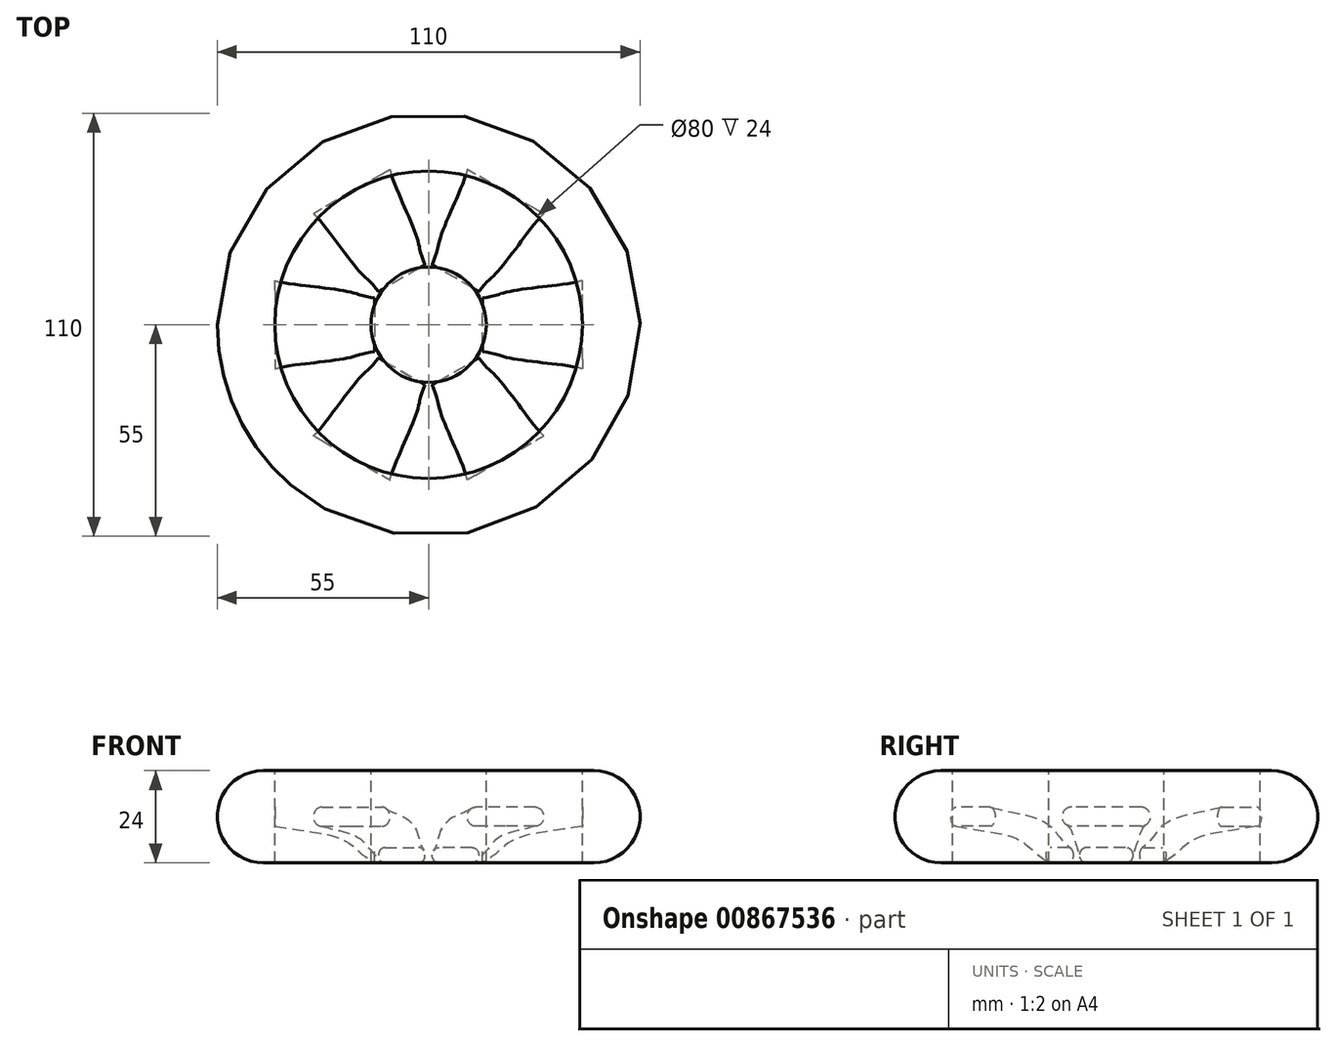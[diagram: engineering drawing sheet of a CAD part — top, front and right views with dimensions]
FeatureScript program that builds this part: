
annotation { "Feature Type Name" : "Feature", "Feature Type Description" : "" }
export const myFeature = defineFeature(function(context is Context, id is Id, definition is map)
    precondition{}
    {
        {
            var Q0;
            Q0=qCreatedBy(makeId("Top.planeOp"),FACE);
            var sketch = newSketch(context, id + "F0", { "sketchPlane" : qUnion([Q0])});
            skCircle(sketch, "E0", {"center": v(0, 0) * mm, "radius": 40 * mm});
            skSolve(sketch);
        }
        {
            var Q0;
            Q0=qCreatedBy(makeId("Front.planeOp"),FACE);
            var sketch = newSketch(context, id + "F1", { "sketchPlane" : qUnion([Q0])});
            skArc(sketch, "E1", {"start": v(-43, 12) * mm, "mid": v(-55, 0) * mm, "end": v(-43, -12) * mm});
            skLineSegment(sketch, "E2.bottom", {"start": v(-43, 12) * mm, "end": v(-40, 12) * mm});
            skLineSegment(sketch, "E2.top", {"start": v(-43, -12) * mm, "end": v(-40, -12) * mm});
            skLineSegment(sketch, "E2.right", {"start": v(-40, 12) * mm, "end": v(-40, -12) * mm});
            skSolve(sketch);
        }
        {
            var Q0;
            Q0 = qSketchRegion(id + "F1", true);
            var Q1;
            Q1=sQuery(id+"F0.wireOp",EDGE,"E0");
            sweep(context, id + "F2", {"profiles" : qUnion([Q0]), "path" : qUnion([Q1])});
        }
        {
            var Q0;
            Q0=qCreatedBy(makeId("Right.planeOp"),FACE);
            cPlane(context, id + "F3", {"entities" : qUnion([Q0]), "cplaneType" : CPlaneType.OFFSET, "offset" : 40 * mm, "width" : 150 * mm, "height" : 150 * mm});
        }
        {
            var Q0;
            Q0=qCreatedBy(id+"F3.planeOp",FACE);
            var sketch = newSketch(context, id + "F4", { "sketchPlane" : qUnion([Q0])});
            skLineSegment(sketch, "E3", {"start": v(-9, 0) * mm, "end": v(9, 0) * mm});
            skArc(sketch, "E4.0.startCap", {"start": v(-9, -2.5) * mm, "mid": v(-11.5, 0) * mm, "end": v(-9, 2.5) * mm});
            skArc(sketch, "E4.0.endCap", {"start": v(9, 2.5) * mm, "mid": v(11.5, 0) * mm, "end": v(9, -2.5) * mm});
            skLineSegment(sketch, "E4.0.left", {"start": v(-9, 2.5) * mm, "end": v(9, 2.5) * mm});
            skLineSegment(sketch, "E4.0.right", {"start": v(-9, -2.5) * mm, "end": v(9, -2.5) * mm});
            skSolve(sketch);
        }
        {
            var Q0;
            Q0=qCreatedBy(makeId("Right.planeOp"),FACE);
            cPlane(context, id + "F5", {"entities" : qUnion([Q0]), "cplaneType" : CPlaneType.OFFSET, "offset" : 14 * mm, "width" : 150 * mm, "height" : 150 * mm});
        }
        {
            var Q0;
            Q0=qCreatedBy(id+"F5.planeOp",FACE);
            var sketch = newSketch(context, id + "F6", { "sketchPlane" : qUnion([Q0])});
            skLineSegment(sketch, "E5", {"start": v(-5, -10) * mm, "end": v(5, -10) * mm});
            skArc(sketch, "E6.0.startCap", {"start": v(-5, -12) * mm, "mid": v(-7, -10) * mm, "end": v(-5, -8) * mm});
            skArc(sketch, "E6.0.endCap", {"start": v(5, -8) * mm, "mid": v(7, -10) * mm, "end": v(5, -12) * mm});
            skLineSegment(sketch, "E6.0.left", {"start": v(-5, -8) * mm, "end": v(5, -8) * mm});
            skLineSegment(sketch, "E6.0.right", {"start": v(-5, -12) * mm, "end": v(5, -12) * mm});
            skSolve(sketch);
        }
        {
            var Q0;
            Q0=qCreatedBy(makeId("Front.planeOp"),FACE);
            var sketch = newSketch(context, id + "F7", { "sketchPlane" : qUnion([Q0])});
            skFitSpline(sketch, "E7", {"points": [v(40, -2.5) * mm, v(35.5, -3.19) * mm, v(23.17, -5.57) * mm, v(18.78, -8.46) * mm, v(14, -12) * mm], "startDerivative": vector(-12, -0.82) * mm, "endDerivative": vector(-37, -22.75) * mm});
            skSolve(sketch);
        }
        {
            var Q1;
            Q1 = qSketchRegion(id + "F4", true);
            var Q2;
            Q2 = qSketchRegion(id + "F6", true);
            var Q3;
            Q3=sQuery(id+"F7.wireOp",EDGE,"E7");
            loft(context, id + "F8", {"addGuides" : true, "sheetProfilesArray" : [{ "sheetProfileEntities" : qUnion([Q1]) }, { "sheetProfileEntities" : qUnion([Q2]) }], "guidesArray" : [{ "guideEntities" : qUnion([Q3]), "guideDerivativeType" : LoftGuideDerivativeType.DEFAULT, "guideDerivativeMagnitude" : 1 }]});
        }
        {
            var Q0;
            Q0=qCreatedBy(makeId("Front.planeOp"),FACE);
            var sketch = newSketch(context, id + "F9", { "sketchPlane" : qUnion([Q0])});
            skLineSegment(sketch, "E8.bottom", {"start": v(0, -12) * mm, "end": v(15, -12) * mm});
            skLineSegment(sketch, "E8.top", {"start": v(0, 12) * mm, "end": v(15, 12) * mm});
            skLineSegment(sketch, "E8.left", {"start": v(0, 12) * mm, "end": v(0, -12) * mm});
            skLineSegment(sketch, "E8.right", {"start": v(15, 12) * mm, "end": v(15, -12) * mm});
            skSolve(sketch);
        }
        {
            var Q0;
            Q0=makeQuery(id+"F9.imprint","IMPRINT",FACE,{"disambiguationData":[TD([[makeQuery(id+"F9.imprint","IMPRINT",EDGE,{"derivedFrom":sQuery(id+"F9.wireOp",EDGE,"E8.bottom")}),1.0]])]});
            var Q1;
            Q1=sQuery(id+"F9.wireOp",EDGE,"E8.left");
            revolve(context, id + "F10", {"surfaceOperationType" : NewSurfaceOperationType.NEW, "entities" : qUnion([Q0]), "axis" : qUnion([Q1]), "revolveType" : RevolveType.FULL});
        }
        {
            var Q0;
            Q0=makeQuery(id+"F8.opLoft","SWEPT_BODY",BODY,{"disambiguationData":[OSD([makeQuery(id+"F4.imprint","IMPRINT",FACE,{"disambiguationData":[TD([[makeQuery(id+"F4.imprint","IMPRINT",EDGE,{"derivedFrom":sQuery(id+"F4.wireOp",EDGE,"E4.0.startCap")}),-1.0]])]}),makeQuery(id+"F6.imprint","IMPRINT",FACE,{"disambiguationData":[TD([[makeQuery(id+"F6.imprint","IMPRINT",EDGE,{"derivedFrom":sQuery(id+"F6.wireOp",EDGE,"E6.0.startCap")}),-1.0]])]}),sQuery(id+"F7.wireOp",EDGE,"E7")])]});
            var Q1;
            Q1=makeQuery(id+"F10.opRevolve","SWEPT_FACE",FACE,{"disambiguationData":[OSD([sQuery(id+"F9.wireOp",EDGE,"E8.right")])]});
            circularPattern(context, id + "F11", {"entities" : qUnion([Q0]), "axis" : qUnion([Q1]), "angle" : 360 * degree, "instanceCount" : 6, "equalSpace" : true});
        }
        {
            var Q0;
            Q0=makeQuery(id+"F10.opRevolve","SWEPT_FACE",FACE,{"disambiguationData":[OSD([sQuery(id+"F9.wireOp",EDGE,"E8.top")])]});
            var sketch = newSketch(context, id + "F12", { "sketchPlane" : qUnion([Q0])});
            skPoint(sketch, "E9", {"position": v(0, 0) * mm});
            skSolve(sketch);
        }
        {
            var Q0;
            Q0=sQuery(id+"F12.wireOp",VERTEX,"E9");
            var Q1;
            Q1=makeQuery(id+"F2.opSweep","SWEPT_BODY",BODY,{"disambiguationData":[OSD([sQuery(id+"F0.wireOp",EDGE,"E0"),sQuery(id+"F1.wireOp",EDGE,"E1"),sQuery(id+"F1.wireOp",EDGE,"E2.bottom"),sQuery(id+"F1.wireOp",EDGE,"E2.top"),sQuery(id+"F1.wireOp",EDGE,"E2.right")])]});
            hole(context, id + "F13", {"style" : HoleStyle.SIMPLE, "endStyle" : HoleEndStyle.THROUGH, "holeDiameter" : 8 * mm, "majorDiameter" : 5 * mm, "isTappedThrough" : true, "tappedDepth" : 12 * mm, "tapClearance" : 3, "locations" : qUnion([Q0]), "scope" : qUnion([Q1])});
        }
    });
